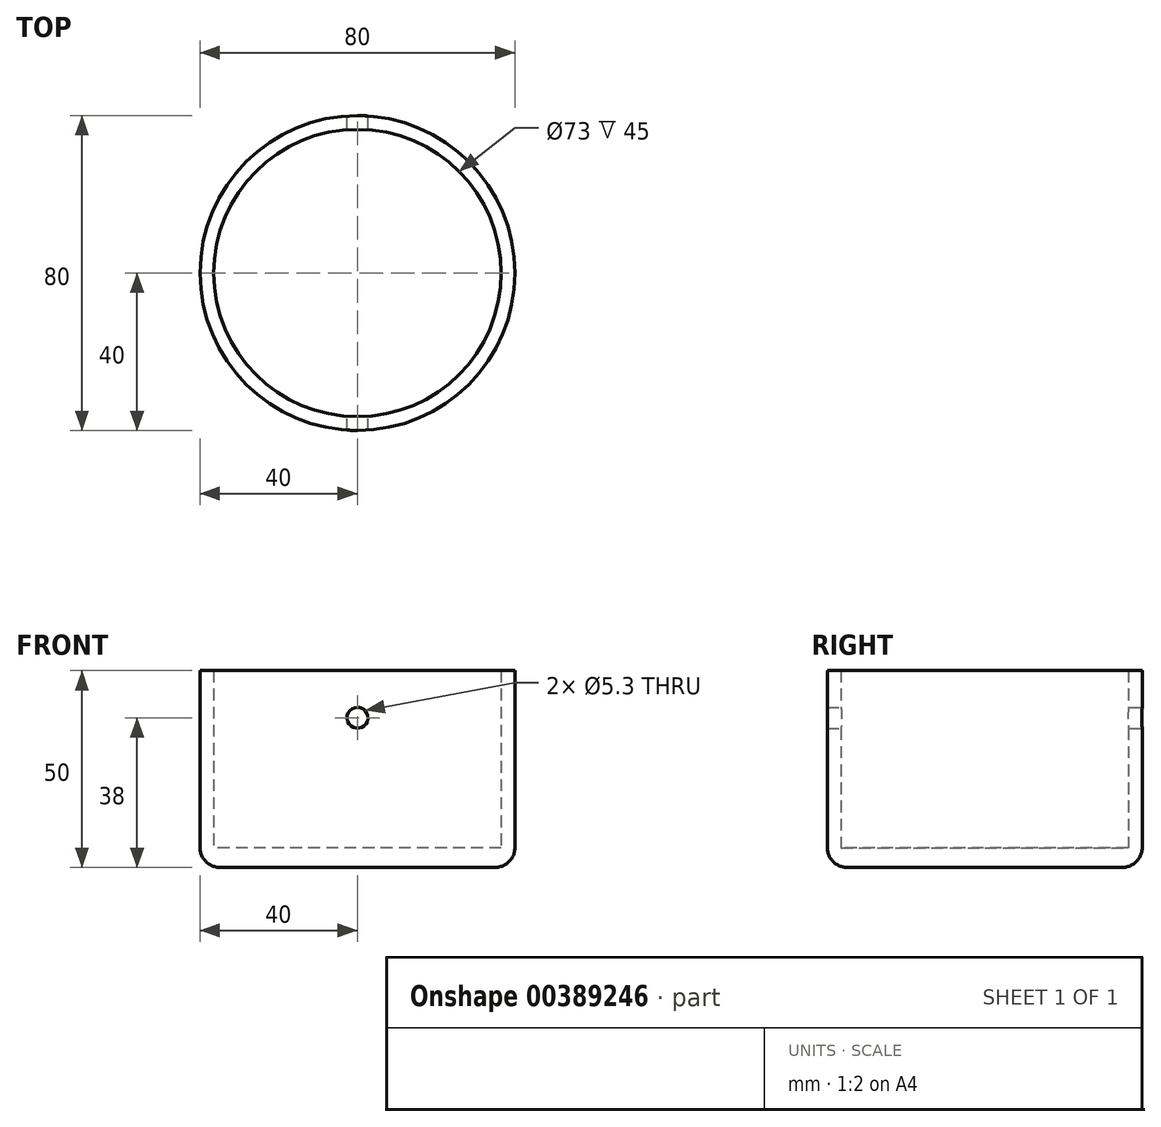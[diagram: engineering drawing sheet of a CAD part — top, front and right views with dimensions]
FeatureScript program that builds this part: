
annotation { "Feature Type Name" : "Feature", "Feature Type Description" : "" }
export const myFeature = defineFeature(function(context is Context, id is Id, definition is map)
    precondition{}
    {
        {
            var Q0;
            Q0=qCreatedBy(makeId("Top.planeOp"),FACE);
            var sketch = newSketch(context, id + "F0", { "sketchPlane" : qUnion([Q0])});
            skCircle(sketch, "E0", {"center": v(0, 0) * mm, "radius": 36.5 * mm});
            skCircle(sketch, "E1", {"center": v(0, 0) * mm, "radius": 40 * mm});
            skSolve(sketch);
        }
        {
            var Q0;
            Q0 = qSketchRegion(id + "F0", true);
            var Q1;
            Q1=makeQuery(id+"F0.imprint","IMPRINT",FACE,{"disambiguationData":[TD([[makeQuery(id+"F0.imprint","IMPRINT",EDGE,{"derivedFrom":sQuery(id+"F0.wireOp",EDGE,"E0")}),1.0]])]});
            extrude(context, id + "F1", {"entities" : qUnion([Q0, Q1]), "depth" : 5 * mm, "offsetDistance" : 25 * mm});
        }
        {
            var Q0;
            Q0=makeQuery(id+"F0.imprint","IMPRINT",FACE,{"disambiguationData":[TD([[makeQuery(id+"F0.imprint","IMPRINT",EDGE,{"derivedFrom":sQuery(id+"F0.wireOp",EDGE,"E0")}),-1.0]])]});
            extrude(context, id + "F2", {"entities" : qUnion([Q0]), "operationType" : NewBodyOperationType.ADD, "depth" : 50 * mm, "offsetDistance" : 25 * mm});
        }
        {
            var Q0;
            Q0=qCreatedBy(makeId("Front.planeOp"),FACE);
            var sketch = newSketch(context, id + "F3", { "sketchPlane" : qUnion([Q0])});
            skCircle(sketch, "E2", {"center": v(0, 38) * mm, "radius": 2.65 * mm});
            skSolve(sketch);
        }
        {
            var Q0;
            Q0 = qSketchRegion(id + "F3", true);
            extrude(context, id + "F4", {"entities" : qUnion([Q0]), "operationType" : NewBodyOperationType.REMOVE, "depth" : 150 * mm, "offsetDistance" : 25 * mm, "symmetric" : true});
        }
        {
            var Q0;
            Q0=makeQuery(id+"F1.opExtrude","CAP_EDGE",EDGE,{"disambiguationData":[OSD([sQuery(id+"F0.wireOp",EDGE,"E1")])],"isStart":true});
            fillet(context, id + "F5", {"entities" : qUnion([Q0]), "radius" : 5 * mm, "tangentPropagation" : true, "allowEdgeOverflow" : false});
        }
    });
